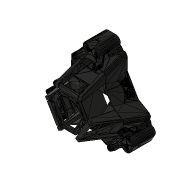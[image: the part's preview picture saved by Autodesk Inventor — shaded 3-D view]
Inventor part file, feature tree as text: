
AUTODESK INVENTOR PART (.ipt)
format: ipt  version: 2019.4 (Build 234330000, 330)  size: 312,832 bytes
history: native  units: mm
features: other x2, sketch x1
ambient origin geometry x8: Origin, YZ Plane, XZ Plane, XY Plane, X Axis, Y Axis, Z Axis, Center Point
feature tree (3):
  other  "00_openflexure_deltastage"
  sketch  "Sketch1"
  other  "MeshFeature1"
